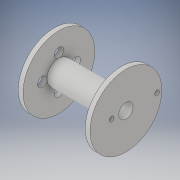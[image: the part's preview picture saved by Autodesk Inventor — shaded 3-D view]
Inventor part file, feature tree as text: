
AUTODESK INVENTOR PART (.ipt)
format: ipt  version: 2019 (Build 230136000, 136)  size: 148,992 bytes
history: native  units: in
note: dims shown in document units (in); Inventor stores cm internally (conversion verified against a paired STEP export)
features: sketch x4, extrude x2, revolve x1
ambient origin geometry x8: Origin, YZ Plane, XZ Plane, XY Plane, X Axis, Y Axis, Z Axis, Center Point
bodies: Solid1 (feature_tree)
feature tree (7):
  revolve  "Revolution1"  [1 undecoded]
  sketch  "Sketch2"  dims[d2=1.0236in d3=0.0787in]
  sketch  "Sketch3"  dims[d4=0.4724in d5=0.1181in]
  extrude  "Extrusion1"  Depth=0.0787in
  extrude  "Extrusion2"  Depth=0.1181in
  sketch  "Sketch1"  dims[d0=0.0787in d1=0.3937in]
  sketch  "Sketch4"  dims[d6=1.1811in d7=90.0deg d8=0.1575in d10=0.1575in d13=0.1575in d14=0.1575in d17=0.2756in d18=0.2756in d19=0.2756in d20=0.2756in d21=0.0787in d22=0.0in d23=0.0787in d24=0.0787in d25=0.2362in d26=0.5118in d27=0.0787in d28=0.0in]
note: 1 required parameter value undecoded (feature->parameter linkage not recoverable at this tier; creation-order binding heuristic only, values carry confidence <= 0.55)
